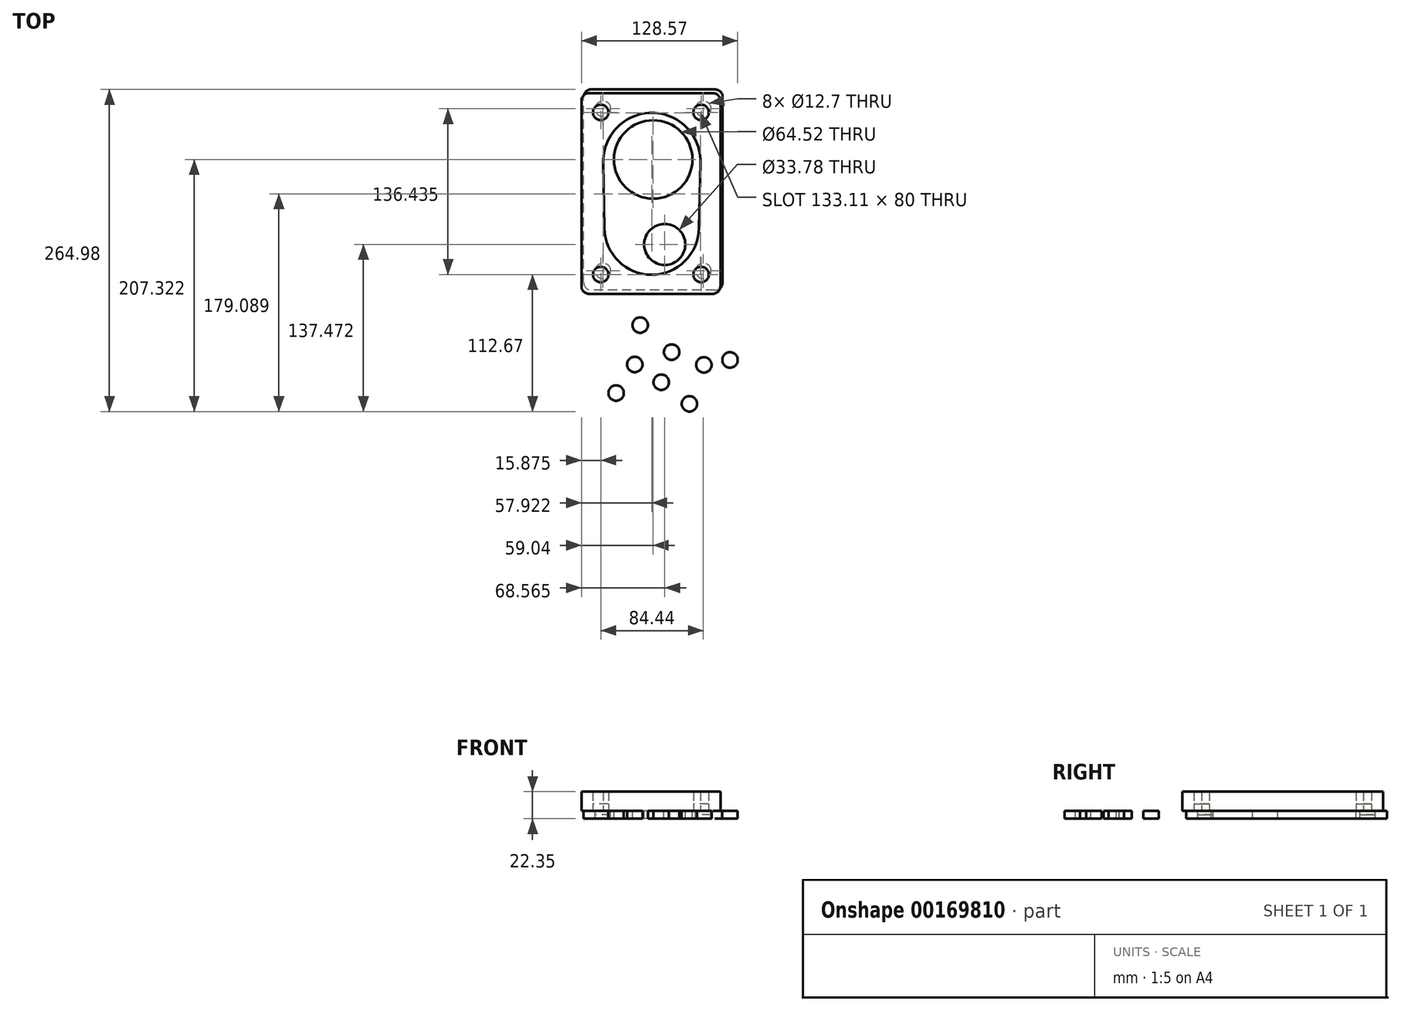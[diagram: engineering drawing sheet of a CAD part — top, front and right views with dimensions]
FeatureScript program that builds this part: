
annotation { "Feature Type Name" : "Feature", "Feature Type Description" : "" }
export const myFeature = defineFeature(function(context is Context, id is Id, definition is map)
    precondition{}
    {
        {
            var Q0;
            Q0=qCreatedBy(makeId("Top.planeOp"),FACE);
            var sketch = newSketch(context, id + "F0", { "sketchPlane" : qUnion([Q0])});
            skLineSegment(sketch, "E0.bottom", {"start": v(50.8, -82.55) * mm, "end": v(-50.8, -82.55) * mm});
            skLineSegment(sketch, "E0.top", {"start": v(50.8, 82.55) * mm, "end": v(-50.8, 82.55) * mm});
            skLineSegment(sketch, "E0.left", {"start": v(57.15, -76.2) * mm, "end": v(57.15, 76.2) * mm});
            skLineSegment(sketch, "E0.right", {"start": v(-57.15, -76.2) * mm, "end": v(-57.15, 76.2) * mm});
            skPoint(sketch, "E0.middle", {"position": v(0, 0) * mm});
            skPoint(sketch, "E1.visualSharp", {"position": v(-57.15, 82.55) * mm});
            skArc(sketch, "E1.filletArc", {"start": v(-50.8, 82.55) * mm, "mid": v(-55.3, 80.7) * mm, "end": v(-57.15, 76.2) * mm});
            skPoint(sketch, "E2.visualSharp", {"position": v(57.15, 82.55) * mm});
            skArc(sketch, "E2.filletArc", {"start": v(57.15, 76.2) * mm, "mid": v(55.3, 80.7) * mm, "end": v(50.8, 82.55) * mm});
            skPoint(sketch, "E3.visualSharp", {"position": v(57.15, -82.55) * mm});
            skArc(sketch, "E3.filletArc", {"start": v(50.8, -82.55) * mm, "mid": v(55.3, -80.7) * mm, "end": v(57.15, -76.2) * mm});
            skPoint(sketch, "E4.visualSharp", {"position": v(-57.15, -82.55) * mm});
            skArc(sketch, "E4.filletArc", {"start": v(-57.15, -76.2) * mm, "mid": v(-55.3, -80.7) * mm, "end": v(-50.8, -82.55) * mm});
            skCircle(sketch, "E5", {"center": v(41.27, 66.68) * mm, "radius": 6.35 * mm});
            skCircle(sketch, "E6", {"center": v(-41.27, -66.68) * mm, "radius": 6.35 * mm});
            skCircle(sketch, "E7", {"center": v(-41.27, 66.68) * mm, "radius": 6.35 * mm});
            skCircle(sketch, "E8", {"center": v(41.28, -66.68) * mm, "radius": 6.35 * mm});
            skCircle(sketch, "E9", {"center": v(0, 24.9) * mm, "radius": 32.26 * mm});
            skCircle(sketch, "E10", {"center": v(9.53, -44.96) * mm, "radius": 16.9 * mm});
            skSolve(sketch);
        }
        {
            var Q0;
            Q0=qCreatedBy(makeId("Top.planeOp"),FACE);
            var sketch = newSketch(context, id + "F1", { "sketchPlane" : qUnion([Q0])});
            skLineSegment(sketch, "E11.bottom", {"start": v(48.9, -85.64) * mm, "end": v(-52.7, -85.64) * mm});
            skLineSegment(sketch, "E11.top", {"start": v(48.9, 79.46) * mm, "end": v(-52.7, 79.46) * mm});
            skLineSegment(sketch, "E11.left", {"start": v(55.26, -79.29) * mm, "end": v(55.26, 73.11) * mm});
            skLineSegment(sketch, "E11.right", {"start": v(-59.04, -79.29) * mm, "end": v(-59.04, 73.11) * mm});
            skPoint(sketch, "E11.middle", {"position": v(-1.9, -3.09) * mm});
            skPoint(sketch, "E12.visualSharp", {"position": v(-59.04, 79.46) * mm});
            skArc(sketch, "E12.filletArc", {"start": v(-52.7, 79.46) * mm, "mid": v(-57.18, 77.6) * mm, "end": v(-59.04, 73.11) * mm});
            skPoint(sketch, "E13.visualSharp", {"position": v(55.26, 79.46) * mm});
            skArc(sketch, "E13.filletArc", {"start": v(55.26, 73.11) * mm, "mid": v(53.4, 77.6) * mm, "end": v(48.9, 79.46) * mm});
            skPoint(sketch, "E14.visualSharp", {"position": v(55.26, -85.64) * mm});
            skArc(sketch, "E14.filletArc", {"start": v(48.9, -85.64) * mm, "mid": v(53.4, -83.78) * mm, "end": v(55.26, -79.29) * mm});
            skPoint(sketch, "E15.visualSharp", {"position": v(-59.04, -85.64) * mm});
            skArc(sketch, "E15.filletArc", {"start": v(-59.04, -79.29) * mm, "mid": v(-57.18, -83.78) * mm, "end": v(-52.7, -85.64) * mm});
            skCircle(sketch, "E16", {"center": v(39.38, 63.59) * mm, "radius": 6.35 * mm});
            skCircle(sketch, "E17", {"center": v(-43.17, -69.76) * mm, "radius": 6.35 * mm});
            skCircle(sketch, "E18", {"center": v(-43.17, 63.59) * mm, "radius": 6.35 * mm});
            skCircle(sketch, "E19", {"center": v(39.38, -69.76) * mm, "radius": 6.35 * mm});
            skArc(sketch, "E20", {"start": v(38.88, 22.3) * mm, "mid": v(-1.12, 63.21) * mm, "end": v(-41.12, 22.3) * mm});
            skArc(sketch, "E21", {"start": v(-40.17, -31.66) * mm, "mid": v(-1.25, -69.9) * mm, "end": v(37.67, -31.66) * mm});
            skLineSegment(sketch, "E22", {"start": v(38.88, 22.3) * mm, "end": v(37.67, -31.66) * mm});
            skLineSegment(sketch, "E23", {"start": v(-41.12, 22.3) * mm, "end": v(-40.17, -31.66) * mm});
            skSolve(sketch);
        }
        {
            var Q0;
            Q0=makeQuery(id+"F0.imprint","IMPRINT",FACE,{"disambiguationData":[TD([[makeQuery(id+"F0.imprint","IMPRINT",EDGE,{"derivedFrom":sQuery(id+"F0.wireOp",EDGE,"E6")}),1.0]])]});
            var Q1;
            Q1=makeQuery(id+"F0.imprint","IMPRINT",FACE,{"disambiguationData":[TD([[makeQuery(id+"F0.imprint","IMPRINT",EDGE,{"derivedFrom":sQuery(id+"F0.wireOp",EDGE,"E7")}),1.0]])]});
            var Q2;
            Q2=makeQuery(id+"F0.imprint","IMPRINT",FACE,{"disambiguationData":[TD([[makeQuery(id+"F0.imprint","IMPRINT",EDGE,{"derivedFrom":sQuery(id+"F0.wireOp",EDGE,"E5")}),1.0]])]});
            var Q3;
            Q3=makeQuery(id+"F0.imprint","IMPRINT",FACE,{"disambiguationData":[TD([[makeQuery(id+"F0.imprint","IMPRINT",EDGE,{"derivedFrom":sQuery(id+"F0.wireOp",EDGE,"E8")}),1.0]])]});
            var Q4;
            Q4=sQuery(id+"F0.wireOp",EDGE,"E7");
            var Q5;
            Q5=sQuery(id+"F0.wireOp",EDGE,"E5");
            var Q6;
            Q6=sQuery(id+"F0.wireOp",EDGE,"E8");
            var Q7;
            Q7=sQuery(id+"F0.wireOp",EDGE,"E6");
            extrude(context, id + "F2", {"entities" : qUnion([Q0, Q1, Q2, Q3]), "surfaceEntities" : qUnion([Q4, Q5, Q6, Q7]), "oppositeDirection" : true, "depth" : 3.17 * mm});
        }
        {
            var Q0;
            Q0=makeQuery(id+"F0.imprint","IMPRINT",FACE,{"disambiguationData":[TD([[makeQuery(id+"F0.imprint","IMPRINT",EDGE,{"derivedFrom":sQuery(id+"F0.wireOp",EDGE,"E0.bottom")}),-1.0]])]});
            extrude(context, id + "F3", {"entities" : qUnion([Q0]), "oppositeDirection" : true, "depth" : 6.35 * mm});
        }
        {
            var Q0;
            Q0=makeQuery(id+"F1.imprint","IMPRINT",FACE,{"disambiguationData":[TD([[makeQuery(id+"F1.imprint","IMPRINT",EDGE,{"derivedFrom":sQuery(id+"F1.wireOp",EDGE,"E16")}),1.0]])]});
            var Q1;
            Q1=makeQuery(id+"F1.imprint","IMPRINT",FACE,{"disambiguationData":[TD([[makeQuery(id+"F1.imprint","IMPRINT",EDGE,{"derivedFrom":sQuery(id+"F1.wireOp",EDGE,"E18")}),1.0]])]});
            var Q2;
            Q2=makeQuery(id+"F1.imprint","IMPRINT",FACE,{"disambiguationData":[TD([[makeQuery(id+"F1.imprint","IMPRINT",EDGE,{"derivedFrom":sQuery(id+"F1.wireOp",EDGE,"E17")}),1.0]])]});
            var Q3;
            Q3=makeQuery(id+"F1.imprint","IMPRINT",FACE,{"disambiguationData":[TD([[makeQuery(id+"F1.imprint","IMPRINT",EDGE,{"derivedFrom":sQuery(id+"F1.wireOp",EDGE,"E19")}),1.0]])]});
            extrude(context, id + "F4", {"entities" : qUnion([Q0, Q1, Q2, Q3]), "depth" : 5.84 * mm});
        }
        {
            var Q0;
            Q0=makeQuery(id+"F1.imprint","IMPRINT",FACE,{"disambiguationData":[TD([[makeQuery(id+"F1.imprint","IMPRINT",EDGE,{"derivedFrom":sQuery(id+"F1.wireOp",EDGE,"E11.bottom")}),-1.0]])]});
            extrude(context, id + "F5", {"entities" : qUnion([Q0]), "depth" : 16 * mm});
        }
        {
            var Q0;
            Q0=qCreatedBy(makeId("Top.planeOp"),FACE);
            var sketch = newSketch(context, id + "F6", { "sketchPlane" : qUnion([Q0])});
            skCircle(sketch, "E24", {"center": v(63.18, -139.98) * mm, "radius": 6.35 * mm});
            skCircle(sketch, "E25", {"center": v(41.72, -144.07) * mm, "radius": 6.35 * mm});
            skCircle(sketch, "E26", {"center": v(15.16, -133.5) * mm, "radius": 6.35 * mm});
            skCircle(sketch, "E27", {"center": v(6.64, -158.37) * mm, "radius": 6.35 * mm});
            skCircle(sketch, "E28", {"center": v(-15.16, -143.72) * mm, "radius": 6.35 * mm});
            skCircle(sketch, "E29", {"center": v(-10.73, -111.37) * mm, "radius": 6.35 * mm});
            skCircle(sketch, "E30", {"center": v(-30.48, -167.22) * mm, "radius": 6.35 * mm});
            skCircle(sketch, "E31", {"center": v(29.8, -176.08) * mm, "radius": 6.35 * mm});
            skSolve(sketch);
        }
        {
            var Q0;
            Q0=makeQuery(id+"F6.imprint","IMPRINT",FACE,{"disambiguationData":[TD([[makeQuery(id+"F6.imprint","IMPRINT",EDGE,{"derivedFrom":sQuery(id+"F6.wireOp",EDGE,"E31")}),1.0]])]});
            var Q1;
            Q1=makeQuery(id+"F6.imprint","IMPRINT",FACE,{"disambiguationData":[TD([[makeQuery(id+"F6.imprint","IMPRINT",EDGE,{"derivedFrom":sQuery(id+"F6.wireOp",EDGE,"E24")}),1.0]])]});
            var Q2;
            Q2=makeQuery(id+"F6.imprint","IMPRINT",FACE,{"disambiguationData":[TD([[makeQuery(id+"F6.imprint","IMPRINT",EDGE,{"derivedFrom":sQuery(id+"F6.wireOp",EDGE,"E25")}),1.0]])]});
            var Q3;
            Q3=makeQuery(id+"F6.imprint","IMPRINT",FACE,{"disambiguationData":[TD([[makeQuery(id+"F6.imprint","IMPRINT",EDGE,{"derivedFrom":sQuery(id+"F6.wireOp",EDGE,"E27")}),1.0]])]});
            var Q4;
            Q4=makeQuery(id+"F6.imprint","IMPRINT",FACE,{"disambiguationData":[TD([[makeQuery(id+"F6.imprint","IMPRINT",EDGE,{"derivedFrom":sQuery(id+"F6.wireOp",EDGE,"E30")}),1.0]])]});
            var Q5;
            Q5=makeQuery(id+"F6.imprint","IMPRINT",FACE,{"disambiguationData":[TD([[makeQuery(id+"F6.imprint","IMPRINT",EDGE,{"derivedFrom":sQuery(id+"F6.wireOp",EDGE,"E28")}),1.0]])]});
            var Q6;
            Q6=makeQuery(id+"F6.imprint","IMPRINT",FACE,{"disambiguationData":[TD([[makeQuery(id+"F6.imprint","IMPRINT",EDGE,{"derivedFrom":sQuery(id+"F6.wireOp",EDGE,"E26")}),1.0]])]});
            var Q7;
            Q7=makeQuery(id+"F6.imprint","IMPRINT",FACE,{"disambiguationData":[TD([[makeQuery(id+"F6.imprint","IMPRINT",EDGE,{"derivedFrom":sQuery(id+"F6.wireOp",EDGE,"E29")}),1.0]])]});
            var Q8;
            Q8=sQuery(id+"F6.wireOp",EDGE,"E31");
            var Q9;
            Q9=sQuery(id+"F6.wireOp",EDGE,"E25");
            var Q10;
            Q10=sQuery(id+"F6.wireOp",EDGE,"E24");
            var Q11;
            Q11=sQuery(id+"F6.wireOp",EDGE,"E26");
            var Q12;
            Q12=sQuery(id+"F6.wireOp",EDGE,"E27");
            var Q13;
            Q13=sQuery(id+"F6.wireOp",EDGE,"E28");
            var Q14;
            Q14=sQuery(id+"F6.wireOp",EDGE,"E29");
            var Q15;
            Q15=sQuery(id+"F6.wireOp",EDGE,"E30");
            extrude(context, id + "F7", {"entities" : qUnion([Q0, Q1, Q2, Q3, Q4, Q5, Q6, Q7]), "surfaceEntities" : qUnion([Q8, Q9, Q10, Q11, Q12, Q13, Q14, Q15]), "oppositeDirection" : true, "depth" : 6.35 * mm});
        }
    });
